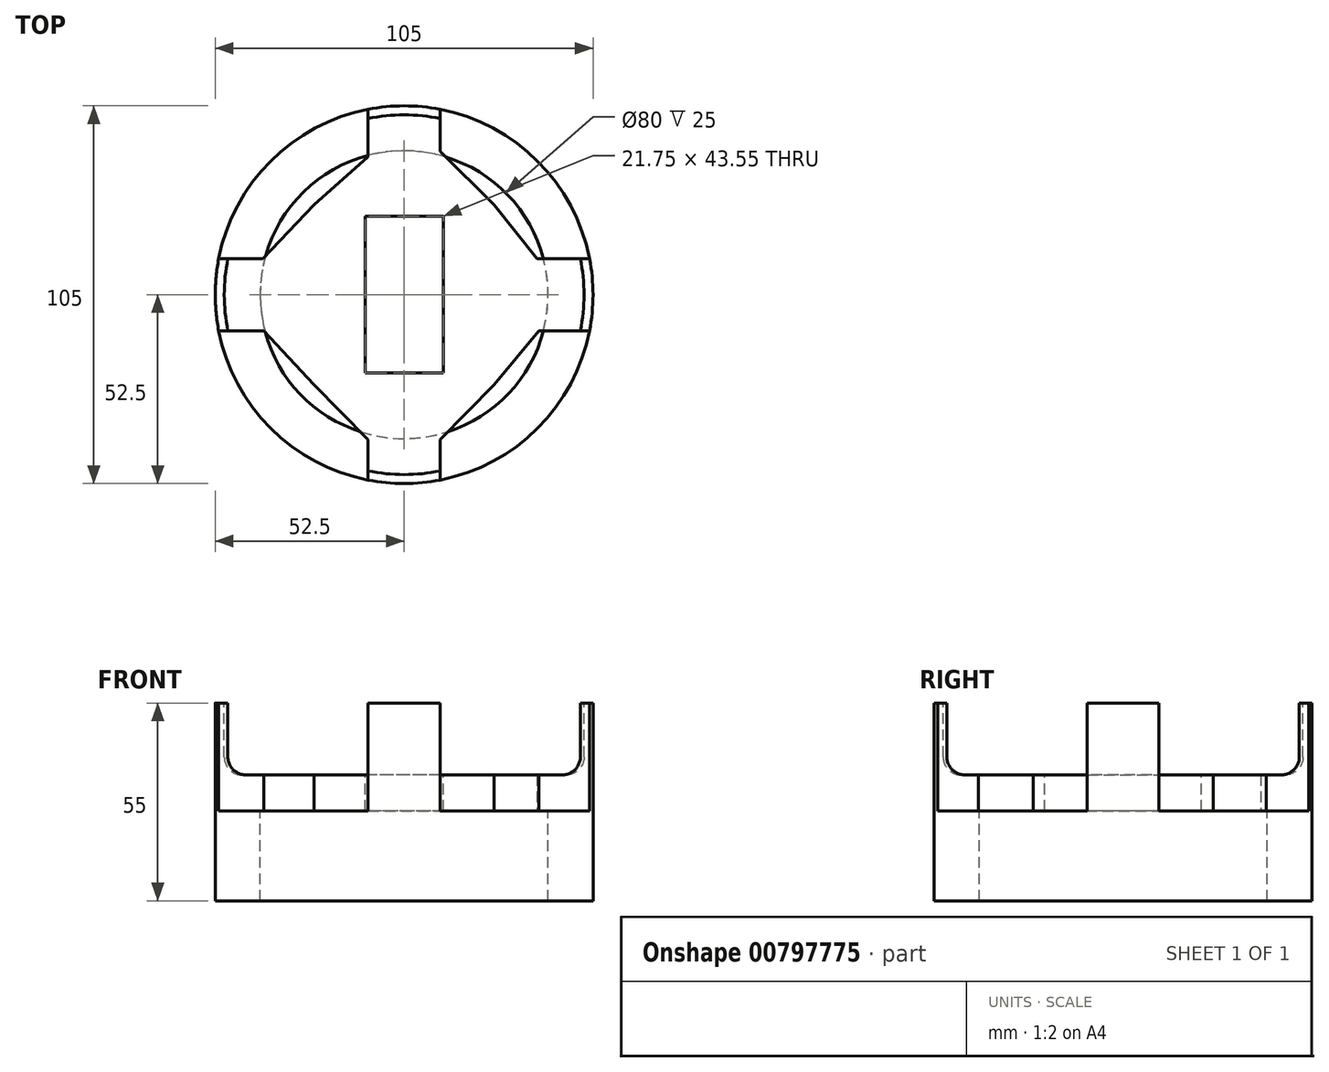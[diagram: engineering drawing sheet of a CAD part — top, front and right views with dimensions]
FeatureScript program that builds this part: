
annotation { "Feature Type Name" : "Feature", "Feature Type Description" : "" }
export const myFeature = defineFeature(function(context is Context, id is Id, definition is map)
    precondition{}
    {
        {
            var Q0;
            Q0=qCreatedBy(makeId("Top.planeOp"),FACE);
            var sketch = newSketch(context, id + "F0", { "sketchPlane" : qUnion([Q0])});
            skCircle(sketch, "E0", {"center": v(0, 0) * mm, "radius": 52.5 * mm});
            skSolve(sketch);
        }
        {
            var Q0;
            Q0=makeQuery(id+"F0.imprint","IMPRINT",FACE,{"disambiguationData":[TD([[makeQuery(id+"F0.imprint","IMPRINT",EDGE,{"derivedFrom":sQuery(id+"F0.wireOp",EDGE,"E0")}),1.0]])]});
            extrude(context, id + "F1", {"entities" : qUnion([Q0]), "depth" : 20 * mm, "offsetDistance" : 25 * mm});
        }
        {
            var Q0;
            Q0=makeQuery(id+"F1.opExtrude","CAP_FACE",FACE,{"disambiguationData":[OSD([sQuery(id+"F0.wireOp",EDGE,"E0")])],"isStart":false});
            var sketch = newSketch(context, id + "F2", { "sketchPlane" : qUnion([Q0])});
            skCircle(sketch, "E1", {"center": v(0, 0) * mm, "radius": 50 * mm});
            skSolve(sketch);
        }
        {
            var Q0;
            Q0=makeQuery(id+"F2.imprint","IMPRINT",FACE,{"disambiguationData":[TD([[makeQuery(id+"F2.imprint","IMPRINT",EDGE,{"derivedFrom":sQuery(id+"F2.wireOp",EDGE,"E1")}),1.0]])]});
            extrude(context, id + "F3", {"entities" : qUnion([Q0]), "operationType" : NewBodyOperationType.REMOVE, "oppositeDirection" : true, "depth" : 10 * mm, "offsetDistance" : 25 * mm});
        }
        {
            var Q0;
            Q0=makeQuery(id+"F3.boolean.opBoolean","COPY",EDGE,{"derivedFrom":makeQuery(id+"F3.opExtrude","CAP_EDGE",EDGE,{"disambiguationData":[OSD([sQuery(id+"F2.wireOp",EDGE,"E1")])],"isStart":false})});
            fillet(context, id + "F4", {"entities" : qUnion([Q0]), "radius" : 5 * mm, "tangentPropagation" : true, "allowEdgeOverflow" : false});
        }
        {
            var Q0;
            Q0=makeQuery(id+"F1.opExtrude","CAP_FACE",FACE,{"disambiguationData":[OSD([sQuery(id+"F0.wireOp",EDGE,"E0")])],"isStart":true});
            var sketch = newSketch(context, id + "F5", { "sketchPlane" : qUnion([Q0])});
            skLineSegment(sketch, "E2", {"start": v(0, 52.5) * mm, "end": v(0, -52.5) * mm});
            skLineSegment(sketch, "E3", {"start": v(52.5, 0) * mm, "end": v(-52.5, 0) * mm});
            skLineSegment(sketch, "E4.0", {"start": v(52.5, 10) * mm, "end": v(37.43, 10) * mm});
            skLineSegment(sketch, "E5.0", {"start": v(52.5, -10) * mm, "end": v(37, -10) * mm});
            skLineSegment(sketch, "E6.0", {"start": v(10, 52.5) * mm, "end": v(10, -39.82) * mm});
            skLineSegment(sketch, "E7.0", {"start": v(-10, 52.5) * mm, "end": v(-10, -38.3) * mm});
            skLineSegment(sketch, "E8.bottom", {"start": v(25, 25) * mm, "end": v(-25, 25) * mm});
            skLineSegment(sketch, "E8.top", {"start": v(25, -25) * mm, "end": v(-25, -25) * mm});
            skLineSegment(sketch, "E8.left", {"start": v(25, 25) * mm, "end": v(25, -25) * mm});
            skLineSegment(sketch, "E8.right", {"start": v(-25, 25) * mm, "end": v(-25, -25) * mm});
            skPoint(sketch, "E8.middle", {"position": v(0, 0) * mm});
            skLineSegment(sketch, "E9", {"start": v(10, -39.82) * mm, "end": v(10, -52.5) * mm});
            skLineSegment(sketch, "E10", {"start": v(-10, -38.3) * mm, "end": v(-10, -52.5) * mm});
            skLineSegment(sketch, "E11", {"start": v(-39.27, -10) * mm, "end": v(-52.5, -10) * mm});
            skLineSegment(sketch, "E12", {"start": v(-38.97, 10) * mm, "end": v(-52.5, 10) * mm});
            skLineSegment(sketch, "E13", {"start": v(37.43, 10) * mm, "end": v(-38.97, 10) * mm});
            skLineSegment(sketch, "E14", {"start": v(37, -10) * mm, "end": v(-39.27, -10) * mm});
            skLineSegment(sketch, "E15", {"start": v(37, -10) * mm, "end": v(25, -25) * mm});
            skLineSegment(sketch, "E16", {"start": v(37.43, 10) * mm, "end": v(25, 25) * mm});
            skLineSegment(sketch, "E17", {"start": v(-38.97, 10) * mm, "end": v(-25, 25) * mm});
            skLineSegment(sketch, "E18", {"start": v(-39.27, -10) * mm, "end": v(-25, -25) * mm});
            skLineSegment(sketch, "E19", {"start": v(-25, -25) * mm, "end": v(-10, -38.3) * mm});
            skLineSegment(sketch, "E20", {"start": v(10, -39.82) * mm, "end": v(25, -25) * mm});
            skLineSegment(sketch, "E21", {"start": v(25, 25) * mm, "end": v(10, 40.28) * mm});
            skLineSegment(sketch, "E22", {"start": v(-10, 40.28) * mm, "end": v(-25, 25) * mm});
            skSolve(sketch);
        }
        {
            var Q0;
            {var subQ0=sQuery(id+"F5.wireOp",EDGE,"E8.right");var subQ3=sQuery(id+"F5.wireOp",EDGE,"E5.0");var subQ4=makeQuery(id+"F5.imprint","INTERSECT",VERTEX,{"derivedFrom":[subQ3,subQ0]});Q0=makeQuery(id+"F5.imprint","IMPRINT",FACE,{"disambiguationData":[TD([[makeQuery(id+"F5.imprint","IMPRINT",EDGE,{"disambiguationData":[TD([[subQ4,-1.0]])],"derivedFrom":subQ3}),1.0]])]});}
            var Q1;
            {var subQ0=sQuery(id+"F5.wireOp",EDGE,"E8.right");var subQ3=sQuery(id+"F5.wireOp",EDGE,"E4.0");var subQ4=makeQuery(id+"F5.imprint","INTERSECT",VERTEX,{"derivedFrom":[subQ3,subQ0]});Q1=makeQuery(id+"F5.imprint","IMPRINT",FACE,{"disambiguationData":[TD([[makeQuery(id+"F5.imprint","IMPRINT",EDGE,{"disambiguationData":[TD([[subQ4,-1.0]])],"derivedFrom":subQ3}),-1.0]])]});}
            var Q2;
            {var subQ0=sQuery(id+"F5.wireOp",EDGE,"E8.left");var subQ5=sQuery(id+"F5.wireOp",EDGE,"E4.0");var subQ6=makeQuery(id+"F5.imprint","INTERSECT",VERTEX,{"derivedFrom":[subQ5,subQ0]});Q2=makeQuery(id+"F5.imprint","IMPRINT",FACE,{"disambiguationData":[TD([[makeQuery(id+"F5.imprint","IMPRINT",EDGE,{"disambiguationData":[TD([[subQ6,1.0]])],"derivedFrom":subQ5}),-1.0]])]});}
            var Q3;
            {var subQ0=sQuery(id+"F5.wireOp",EDGE,"E8.left");var subQ3=sQuery(id+"F5.wireOp",EDGE,"E5.0");var subQ4=makeQuery(id+"F5.imprint","INTERSECT",VERTEX,{"derivedFrom":[subQ3,subQ0]});Q3=makeQuery(id+"F5.imprint","IMPRINT",FACE,{"disambiguationData":[TD([[makeQuery(id+"F5.imprint","IMPRINT",EDGE,{"disambiguationData":[TD([[subQ4,1.0]])],"derivedFrom":subQ3}),1.0]])]});}
            var Q4;
            {var subQ1=sQuery(id+"F5.wireOp",EDGE,"E18");Q4=makeQuery(id+"F5.imprint","IMPRINT",FACE,{"disambiguationData":[TD([[makeQuery(id+"F5.imprint","IMPRINT",EDGE,{"derivedFrom":subQ1}),-1.0]])]});}
            var Q5;
            {var subQ6=sQuery(id+"F5.wireOp",EDGE,"E17");Q5=makeQuery(id+"F5.imprint","IMPRINT",FACE,{"disambiguationData":[TD([[makeQuery(id+"F5.imprint","IMPRINT",EDGE,{"derivedFrom":subQ6}),1.0]])]});}
            extrude(context, id + "F6", {"entities" : qUnion([Q0, Q1, Q2, Q3, Q4, Q5]), "operationType" : NewBodyOperationType.REMOVE, "oppositeDirection" : true, "depth" : 25 * mm, "offsetDistance" : 25 * mm});
        }
        {
            var Q0;
            Q0=makeQuery(id+"F3.boolean.opBoolean","COPY",FACE,{"derivedFrom":makeQuery(id+"F3.opExtrude","CAP_FACE",FACE,{"disambiguationData":[OSD([sQuery(id+"F2.wireOp",EDGE,"E1")])],"isStart":false})});
            var sketch = newSketch(context, id + "F7", { "sketchPlane" : qUnion([Q0])});
            skLineSegment(sketch, "E23.bottom", {"start": v(10.87, 21.78) * mm, "end": v(-10.87, 21.78) * mm});
            skLineSegment(sketch, "E23.top", {"start": v(10.87, -21.78) * mm, "end": v(-10.87, -21.78) * mm});
            skLineSegment(sketch, "E23.left", {"start": v(10.87, 21.78) * mm, "end": v(10.87, -21.78) * mm});
            skLineSegment(sketch, "E23.right", {"start": v(-10.87, 21.78) * mm, "end": v(-10.87, -21.78) * mm});
            skPoint(sketch, "E23.middle", {"position": v(0, 0) * mm});
            skSolve(sketch);
        }
        {
            var Q0;
            Q0 = qSketchRegion(id + "F7", true);
            extrude(context, id + "F8", {"entities" : qUnion([Q0]), "operationType" : NewBodyOperationType.REMOVE, "oppositeDirection" : true, "depth" : 25 * mm, "offsetDistance" : 25 * mm});
        }
        {
            var Q0;
            {var subQ0=sQuery(id+"F0.wireOp",EDGE,"E0");var subQ1=sQuery(id+"F5.wireOp",EDGE,"E8.right");var subQ2=sQuery(id+"F5.wireOp",EDGE,"E4.0");Q0=makeQuery(id+"F6.boolean.opBoolean","SPLIT",FACE,{"disambiguationData":[TD([makeQuery(id+"F6.opExtrude","SWEPT_FACE",FACE,{"disambiguationData":[OSD([subQ2]),TDD([makeQuery(id+"F5.imprint","IMPRINT",EDGE,{"disambiguationData":[TD([[makeQuery(id+"F5.imprint","INTERSECT",VERTEX,{"derivedFrom":[subQ2,subQ1]}),-1.0]])],"derivedFrom":subQ2})])]})])],"derivedFrom":makeQuery(id+"F1.opExtrude","CAP_FACE",FACE,{"disambiguationData":[OSD([subQ0])],"isStart":false})});}
            var Q1;
            {var subQ0=sQuery(id+"F0.wireOp",EDGE,"E0");var subQ1=sQuery(id+"F5.wireOp",EDGE,"E8.bottom");var subQ2=sQuery(id+"F5.wireOp",EDGE,"E6.0");Q1=makeQuery(id+"F6.boolean.opBoolean","SPLIT",FACE,{"disambiguationData":[TD([makeQuery(id+"F6.opExtrude","SWEPT_FACE",FACE,{"disambiguationData":[OSD([subQ2]),TDD([makeQuery(id+"F5.imprint","IMPRINT",EDGE,{"disambiguationData":[TD([[makeQuery(id+"F5.imprint","INTERSECT",VERTEX,{"derivedFrom":[subQ2,subQ1]}),1.0]])],"derivedFrom":subQ2})])]})])],"derivedFrom":makeQuery(id+"F1.opExtrude","CAP_FACE",FACE,{"disambiguationData":[OSD([subQ0])],"isStart":false})});}
            var Q2;
            {var subQ0=sQuery(id+"F0.wireOp",EDGE,"E0");var subQ1=sQuery(id+"F5.wireOp",EDGE,"E8.left");var subQ4=sQuery(id+"F5.wireOp",EDGE,"E4.0");Q2=makeQuery(id+"F6.boolean.opBoolean","SPLIT",FACE,{"disambiguationData":[TD([makeQuery(id+"F6.opExtrude","SWEPT_FACE",FACE,{"disambiguationData":[OSD([subQ4]),TDD([makeQuery(id+"F5.imprint","IMPRINT",EDGE,{"disambiguationData":[TD([[makeQuery(id+"F5.imprint","INTERSECT",VERTEX,{"derivedFrom":[subQ4,subQ1]}),1.0]])],"derivedFrom":subQ4})])]})])],"derivedFrom":makeQuery(id+"F1.opExtrude","CAP_FACE",FACE,{"disambiguationData":[OSD([subQ0])],"isStart":false})});}
            var Q3;
            {var subQ0=sQuery(id+"F0.wireOp",EDGE,"E0");var subQ1=sQuery(id+"F5.wireOp",EDGE,"E8.top");var subQ2=sQuery(id+"F5.wireOp",EDGE,"E6.0");Q3=makeQuery(id+"F6.boolean.opBoolean","SPLIT",FACE,{"disambiguationData":[TD([makeQuery(id+"F6.opExtrude","SWEPT_FACE",FACE,{"disambiguationData":[OSD([subQ2]),TDD([makeQuery(id+"F5.imprint","IMPRINT",EDGE,{"disambiguationData":[TD([[makeQuery(id+"F5.imprint","INTERSECT",VERTEX,{"derivedFrom":[subQ2,subQ1]}),-1.0]])],"derivedFrom":subQ2})])]})])],"derivedFrom":makeQuery(id+"F1.opExtrude","CAP_FACE",FACE,{"disambiguationData":[OSD([subQ0])],"isStart":false})});}
            var Q4;
            {var subQ0=sQuery(id+"F0.wireOp",EDGE,"E0");Q4=makeQuery(id+"F6.boolean.opBoolean","SPLIT",FACE,{"disambiguationData":[TD([makeQuery(id+"F6.opExtrude","SWEPT_FACE",FACE,{"disambiguationData":[OSD([sQuery(id+"F5.wireOp",EDGE,"E9")])]})])],"derivedFrom":makeQuery(id+"F1.opExtrude","CAP_FACE",FACE,{"disambiguationData":[OSD([subQ0])],"isStart":false})});}
            var Q5;
            {var subQ0=sQuery(id+"F0.wireOp",EDGE,"E0");Q5=makeQuery(id+"F6.boolean.opBoolean","SPLIT",FACE,{"disambiguationData":[TD([makeQuery(id+"F6.opExtrude","SWEPT_FACE",FACE,{"disambiguationData":[OSD([sQuery(id+"F5.wireOp",EDGE,"E11")])]})])],"derivedFrom":makeQuery(id+"F1.opExtrude","CAP_FACE",FACE,{"disambiguationData":[OSD([subQ0])],"isStart":false})});}
            extrude(context, id + "F9", {"entities" : qUnion([Q0, Q1, Q2, Q3, Q4, Q5]), "operationType" : NewBodyOperationType.ADD, "depth" : 10 * mm, "offsetDistance" : 25 * mm});
        }
        {
            var Q0;
            Q0=makeQuery(id+"F1.opExtrude","CAP_FACE",FACE,{"disambiguationData":[OSD([sQuery(id+"F0.wireOp",EDGE,"E0")])],"isStart":true});
            var sketch = newSketch(context, id + "F10", { "sketchPlane" : qUnion([Q0])});
            skCircle(sketch, "E24", {"center": v(0, 0) * mm, "radius": 52.5 * mm});
            skCircle(sketch, "E25", {"center": v(0, 0) * mm, "radius": 40 * mm});
            skSolve(sketch);
        }
        {
            var Q0;
            Q0 = qSketchRegion(id + "F10", true);
            extrude(context, id + "F11", {"entities" : qUnion([Q0]), "operationType" : NewBodyOperationType.ADD, "depth" : 25 * mm, "offsetDistance" : 25 * mm});
        }
    });
